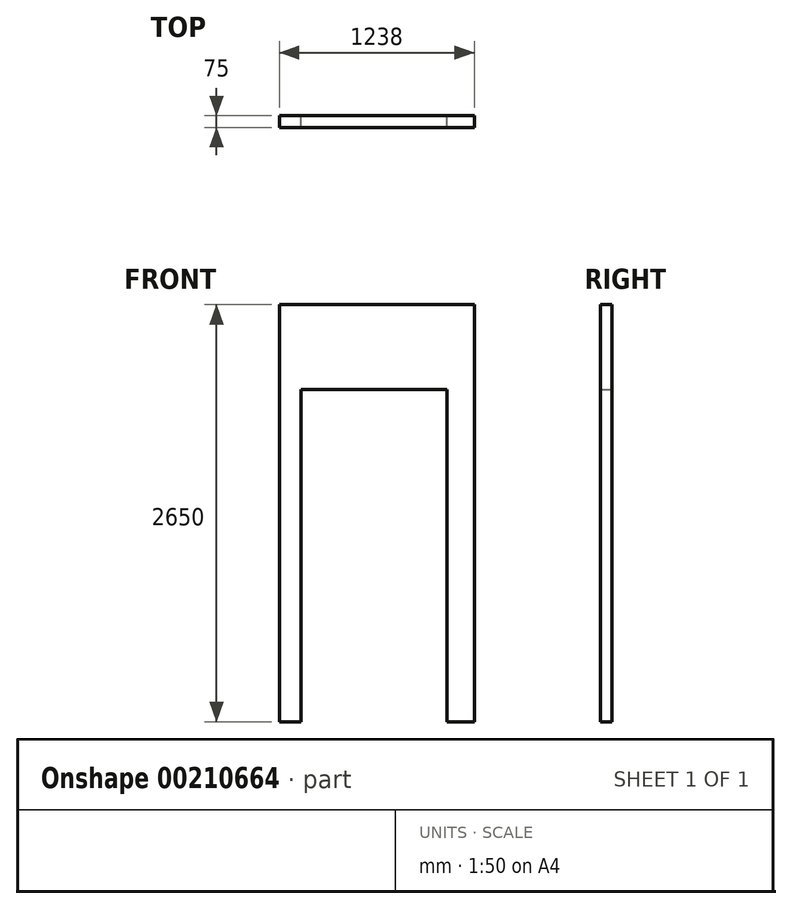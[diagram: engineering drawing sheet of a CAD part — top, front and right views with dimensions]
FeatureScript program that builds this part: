
annotation { "Feature Type Name" : "Feature", "Feature Type Description" : "" }
export const myFeature = defineFeature(function(context is Context, id is Id, definition is map)
    precondition{}
    {
        {
            var Q0;
            Q0=qCreatedBy(makeId("Front.planeOp"),FACE);
            var sketch = newSketch(context, id + "F0", { "sketchPlane" : qUnion([Q0])});
            skLineSegment(sketch, "E0.bottom", {"start": v(0, 0) * mm, "end": v(1238, 0) * mm});
            skLineSegment(sketch, "E0.top", {"start": v(0, 2650) * mm, "end": v(1238, 2650) * mm});
            skLineSegment(sketch, "E0.left", {"start": v(0, 0) * mm, "end": v(0, 2650) * mm});
            skLineSegment(sketch, "E0.right", {"start": v(1238, 0) * mm, "end": v(1238, 2650) * mm});
            skLineSegment(sketch, "E1.bottom", {"start": v(138, 0) * mm, "end": v(1063, 0) * mm});
            skLineSegment(sketch, "E1.top", {"start": v(138, 2110) * mm, "end": v(1063, 2110) * mm});
            skLineSegment(sketch, "E1.left", {"start": v(138, 0) * mm, "end": v(138, 2110) * mm});
            skLineSegment(sketch, "E1.right", {"start": v(1063, 0) * mm, "end": v(1063, 2110) * mm});
            skSolve(sketch);
        }
        {
            var Q0;
            Q0=makeQuery(id+"F0.imprint","IMPRINT",FACE,{"disambiguationData":[TD([[makeQuery(id+"F0.imprint","IMPRINT",EDGE,{"derivedFrom":sQuery(id+"F0.wireOp",EDGE,"E0.top")}),-1.0]])]});
            extrude(context, id + "F1", {"entities" : qUnion([Q0]), "depth" : 75 * mm});
        }
    });
